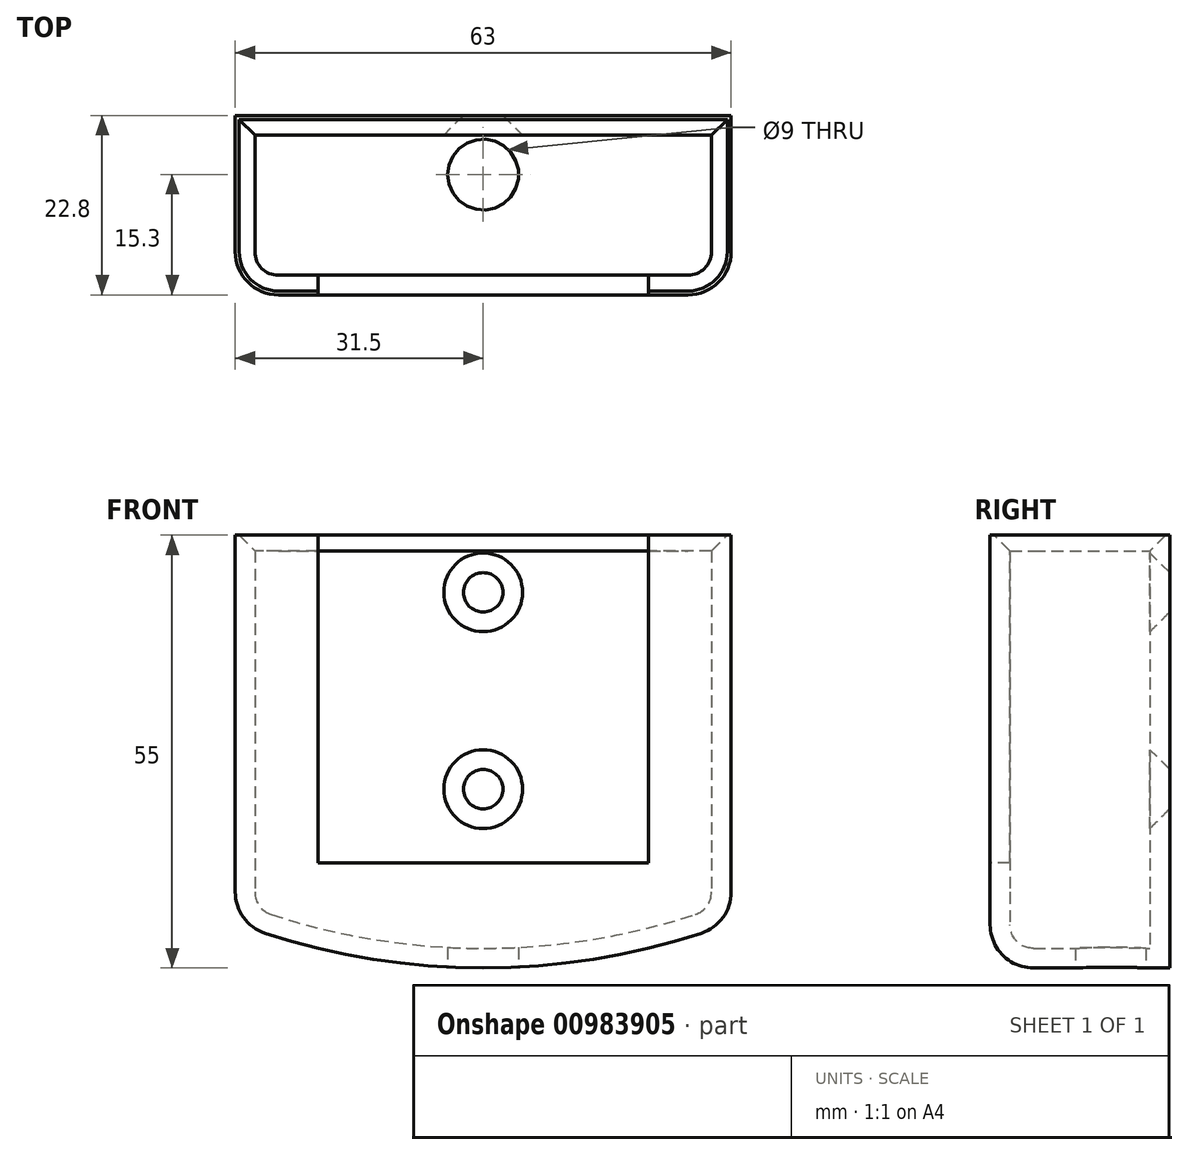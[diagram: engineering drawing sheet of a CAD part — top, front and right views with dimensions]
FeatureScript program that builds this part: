
annotation { "Feature Type Name" : "Feature", "Feature Type Description" : "" }
export const myFeature = defineFeature(function(context is Context, id is Id, definition is map)
    precondition{}
    {
        {
            var Q0;
            Q0=qCreatedBy(makeId("Front.planeOp"),FACE);
            var sketch = newSketch(context, id + "F0", { "sketchPlane" : qUnion([Q0])});
            skLineSegment(sketch, "E0.bottom", {"start": v(29, 25) * mm, "end": v(-29, 25) * mm});
            skLineSegment(sketch, "E0.left", {"start": v(29, 25) * mm, "end": v(29, -25) * mm});
            skLineSegment(sketch, "E0.right", {"start": v(-29, 25) * mm, "end": v(-29, -25) * mm});
            skPoint(sketch, "E0.middle", {"position": v(0, 0) * mm});
            skLineSegment(sketch, "E1", {"start": v(0, -25) * mm, "end": v(0, -30) * mm, "construction": true});
            skArc(sketch, "E2", {"start": v(-29, -25) * mm, "mid": v(0, -30) * mm, "end": v(29, -25) * mm});
            skSolve(sketch);
        }
        {
            var Q0;
            Q0=makeQuery(id+"F0.imprint","IMPRINT",FACE,{"disambiguationData":[TD([[makeQuery(id+"F0.imprint","IMPRINT",EDGE,{"derivedFrom":sQuery(id+"F0.wireOp",EDGE,"E0.bottom")}),1.0]])]});
            extrude(context, id + "F1", {"entities" : qUnion([Q0]), "depth" : 17.8 * mm, "offsetDistance" : 25 * mm});
        }
        {
            var Q0;
            Q0=makeQuery(id+"F1.opExtrude","CAP_EDGE",EDGE,{"disambiguationData":[OSD([sQuery(id+"F0.wireOp",EDGE,"E0.right")])],"isStart":false});
            var Q1;
            Q1=makeQuery(id+"F1.opExtrude","CAP_EDGE",EDGE,{"disambiguationData":[OSD([sQuery(id+"F0.wireOp",EDGE,"E2")])],"isStart":false});
            var Q2;
            Q2=makeQuery(id+"F1.opExtrude","CAP_EDGE",EDGE,{"disambiguationData":[OSD([sQuery(id+"F0.wireOp",EDGE,"E0.left")])],"isStart":false});
            var Q3;
            Q3=makeQuery(id+"F1.opExtrude","SWEPT_EDGE",EDGE,{"disambiguationData":[OSD([sQuery(id+"F0.wireOp",EDGE,"E0.right"),sQuery(id+"F0.wireOp",EDGE,"E2")])]});
            var Q4;
            Q4=makeQuery(id+"F1.opExtrude","SWEPT_EDGE",EDGE,{"disambiguationData":[OSD([sQuery(id+"F0.wireOp",EDGE,"E0.left"),sQuery(id+"F0.wireOp",EDGE,"E2")])]});
            fillet(context, id + "F2", {"entities" : qUnion([Q0, Q1, Q2, Q3, Q4]), "radius" : 3 * mm, "tangentPropagation" : true, "allowEdgeOverflow" : false});
        }
        {
            var Q0;
            Q0=makeQuery(id+"F1.opExtrude","CAP_FACE",FACE,{"disambiguationData":[OSD([sQuery(id+"F0.wireOp",EDGE,"E0.bottom"),sQuery(id+"F0.wireOp",EDGE,"E0.left"),sQuery(id+"F0.wireOp",EDGE,"E0.right"),sQuery(id+"F0.wireOp",EDGE,"E2")])],"isStart":false});
            var Q1;
            Q1=makeQuery(id+"F1.opExtrude","SWEPT_FACE",FACE,{"disambiguationData":[OSD([sQuery(id+"F0.wireOp",EDGE,"E0.bottom")])]});
            var Q2;
            Q2=makeQuery(id+"F1.opExtrude","CAP_FACE",FACE,{"disambiguationData":[OSD([sQuery(id+"F0.wireOp",EDGE,"E0.bottom"),sQuery(id+"F0.wireOp",EDGE,"E0.left"),sQuery(id+"F0.wireOp",EDGE,"E0.right"),sQuery(id+"F0.wireOp",EDGE,"E2")])],"isStart":true});
            var Q3;
            Q3=makeQuery(id+"F2.opFillet","BLEND_FACE",FACE,{"disambiguationData":[OSD([sQuery(id+"F0.wireOp",EDGE,"E2")])]});
            var Q4;
            Q4=makeQuery(id+"F2.opFillet","BLEND_FACE",FACE,{"disambiguationData":[OSD([sQuery(id+"F0.wireOp",EDGE,"E0.right")])]});
            var Q5;
            Q5=makeQuery(id+"F2.opFillet","BLEND_FACE",FACE,{"disambiguationData":[OSD([sQuery(id+"F0.wireOp",EDGE,"E0.left")])]});
            var Q6;
            Q6=makeQuery(id+"F1.opExtrude","SWEPT_FACE",FACE,{"disambiguationData":[OSD([sQuery(id+"F0.wireOp",EDGE,"E0.right")])]});
            var Q7;
            Q7=makeQuery(id+"F1.opExtrude","SWEPT_FACE",FACE,{"disambiguationData":[OSD([sQuery(id+"F0.wireOp",EDGE,"E0.left")])]});
            var Q8;
            Q8=makeQuery(id+"F1.opExtrude","SWEPT_FACE",FACE,{"disambiguationData":[OSD([sQuery(id+"F0.wireOp",EDGE,"E2")])]});
            var Q9;
            Q9=makeQuery(id+"F1.opExtrude","SWEPT_BODY",BODY,{"disambiguationData":[OSD([sQuery(id+"F0.wireOp",EDGE,"E0.bottom"),sQuery(id+"F0.wireOp",EDGE,"E0.left"),sQuery(id+"F0.wireOp",EDGE,"E0.right"),sQuery(id+"F0.wireOp",EDGE,"E2")])]});
            shell(context, id + "F3", {"isHollow" : true, "entities" : qUnion([Q0, Q1, Q2, Q3, Q4, Q5, Q6, Q7, Q8]), "parts" : qUnion([Q9]), "thickness" : 2.5 * mm, "oppositeDirection" : true});
        }
        {
            var Q0;
            Q0=makeQuery(id+"F1.opExtrude","SWEPT_FACE",FACE,{"disambiguationData":[OSD([sQuery(id+"F0.wireOp",EDGE,"E0.bottom")])]});
            extrude(context, id + "F4", {"entities" : qUnion([Q0]), "operationType" : NewBodyOperationType.REMOVE, "oppositeDirection" : true, "depth" : 5 * mm, "offsetDistance" : 25 * mm});
        }
        {
            var Q0;
            {var subQ0=sQuery(id+"F0.wireOp",EDGE,"E0.right");Q0=makeQuery(id+"F4.boolean.opBoolean","INTERSECT",EDGE,{"derivedFrom":[makeQuery(id+"F3.opShell","OFFSET_FACE",FACE,{"disambiguationData":[OSD([subQ0]),TDD([makeQuery(id+"F1.opExtrude","SWEPT_FACE",FACE,{"disambiguationData":[OSD([subQ0])]})])]}),makeQuery(id+"F4.opExtrude","CAP_FACE",FACE,{"disambiguationData":[OSD([sQuery(id+"F0.wireOp",EDGE,"E0.bottom")])],"isStart":false})]});}
            var Q1;
            {var subQ0=sQuery(id+"F0.wireOp",EDGE,"E0.bottom");var subQ1=sQuery(id+"F0.wireOp",EDGE,"E2");var subQ2=sQuery(id+"F0.wireOp",EDGE,"E0.right");var subQ3=sQuery(id+"F0.wireOp",EDGE,"E0.left");Q1=makeQuery(id+"F4.boolean.opBoolean","INTERSECT",EDGE,{"derivedFrom":[makeQuery(id+"F3.opShell","OFFSET_FACE",FACE,{"disambiguationData":[OSD([subQ0,subQ3,subQ2,subQ1]),TDD([makeQuery(id+"F1.opExtrude","CAP_FACE",FACE,{"disambiguationData":[OSD([subQ0,subQ3,subQ2,subQ1])],"isStart":true})])]}),makeQuery(id+"F4.opExtrude","CAP_FACE",FACE,{"disambiguationData":[OSD([subQ0])],"isStart":false})]});}
            chamfer(context, id + "F5", {"entities" : qUnion([Q0, Q1]), "width" : 2 * mm, "tangentPropagation" : true});
        }
        {
            var Q0;
            Q0=makeQuery(id+"F1.opExtrude","CAP_FACE",FACE,{"disambiguationData":[OSD([sQuery(id+"F0.wireOp",EDGE,"E0.bottom"),sQuery(id+"F0.wireOp",EDGE,"E0.left"),sQuery(id+"F0.wireOp",EDGE,"E0.right"),sQuery(id+"F0.wireOp",EDGE,"E2")])],"isStart":false});
            var sketch = newSketch(context, id + "F6", { "sketchPlane" : qUnion([Q0])});
            skLineSegment(sketch, "E3.0.0", {"start": v(26, -22.85) * mm, "end": v(26, 22.5) * mm});
            skLineSegment(sketch, "E3.0.1", {"start": v(26, 22.5) * mm, "end": v(-26, 22.5) * mm});
            skLineSegment(sketch, "E3.0.2", {"start": v(-26, 22.5) * mm, "end": v(-26, -22.85) * mm});
            skArc(sketch, "E3.0.3", {"start": v(-26, -22.85) * mm, "mid": v(0, -27) * mm, "end": v(26, -22.85) * mm});
            skLineSegment(sketch, "E4.0", {"start": v(21, -19.14) * mm, "end": v(21, 22.5) * mm});
            skLineSegment(sketch, "E4.2", {"start": v(-21, 22.5) * mm, "end": v(-21, -19.14) * mm});
            skLineSegment(sketch, "E5", {"start": v(-21, -19.14) * mm, "end": v(21, -19.14) * mm});
            skSolve(sketch);
        }
        {
            var Q0;
            {var subQ0=sQuery(id+"F6.wireOp",EDGE,"E4.0");Q0=makeQuery(id+"F6.imprint","IMPRINT",FACE,{"disambiguationData":[TD([[makeQuery(id+"F6.imprint","IMPRINT",EDGE,{"derivedFrom":subQ0}),1.0]])]});}
            extrude(context, id + "F7", {"entities" : qUnion([Q0]), "operationType" : NewBodyOperationType.REMOVE, "oppositeDirection" : true, "depth" : 6 * mm, "offsetDistance" : 25 * mm});
        }
        {
            var Q0;
            Q0=qCreatedBy(makeId("Top.planeOp"),FACE);
            cPlane(context, id + "F8", {"entities" : qUnion([Q0]), "cplaneType" : CPlaneType.OFFSET, "offset" : 35 * mm, "oppositeDirection" : true, "width" : 150 * mm, "height" : 150 * mm});
        }
        {
            var Q0;
            Q0=qCreatedBy(id+"F8.planeOp",FACE);
            var sketch = newSketch(context, id + "F9", { "sketchPlane" : qUnion([Q0])});
            skLineSegment(sketch, "E6", {"start": v(0, 0) * mm, "end": v(0, -5) * mm, "construction": true});
            skCircle(sketch, "E7", {"center": v(0, -5) * mm, "radius": 4.5 * mm});
            skSolve(sketch);
        }
        {
            var Q0;
            Q0=makeQuery(id+"F9.imprint","IMPRINT",FACE,{"disambiguationData":[TD([[makeQuery(id+"F9.imprint","IMPRINT",EDGE,{"derivedFrom":sQuery(id+"F9.wireOp",EDGE,"E7")}),1.0]])]});
            extrude(context, id + "F10", {"entities" : qUnion([Q0]), "operationType" : NewBodyOperationType.REMOVE, "depth" : 10 * mm, "offsetDistance" : 25 * mm});
        }
        {
            var Q0;
            {var subQ0=sQuery(id+"F0.wireOp",EDGE,"E2");var subQ1=sQuery(id+"F0.wireOp",EDGE,"E0.right");var subQ2=sQuery(id+"F0.wireOp",EDGE,"E0.left");var subQ3=sQuery(id+"F0.wireOp",EDGE,"E0.bottom");Q0=makeQuery(id+"F3.opShell","OFFSET_FACE",FACE,{"disambiguationData":[OSD([subQ3,subQ2,subQ1,subQ0]),TDD([makeQuery(id+"F1.opExtrude","CAP_FACE",FACE,{"disambiguationData":[OSD([subQ3,subQ2,subQ1,subQ0])],"isStart":true})])]});}
            var sketch = newSketch(context, id + "F11", { "sketchPlane" : qUnion([Q0])});
            skLineSegment(sketch, "E8", {"start": v(0, 0) * mm, "end": v(0, 15.22) * mm, "construction": true});
            skLineSegment(sketch, "E9", {"start": v(0, 0) * mm, "end": v(0, -9.78) * mm});
            skSolve(sketch);
        }
        {
            var Q0;
            Q0=sQuery(id+"F11.wireOp",VERTEX,"E8.end");
            var Q1;
            Q1=sQuery(id+"F11.wireOp",VERTEX,"E9.end");
            var Q2;
            Q2=makeQuery(id+"F1.opExtrude","SWEPT_BODY",BODY,{"disambiguationData":[OSD([sQuery(id+"F0.wireOp",EDGE,"E0.bottom"),sQuery(id+"F0.wireOp",EDGE,"E0.left"),sQuery(id+"F0.wireOp",EDGE,"E0.right"),sQuery(id+"F0.wireOp",EDGE,"E2")])]});
            hole(context, id + "F12", {"style" : HoleStyle.C_SINK, "endStyle" : HoleEndStyle.BLIND, "holeDiameter" : 3 * mm, "cSinkDiameter" : 10 * mm, "cSinkAngle" : 90 * degree, "majorDiameter" : 5 * mm, "holeDepth" : 12 * mm, "isTappedThrough" : true, "tappedDepth" : 12 * mm, "tapClearance" : 3, "locations" : qUnion([Q0, Q1]), "scope" : qUnion([Q2])});
        }
    });
